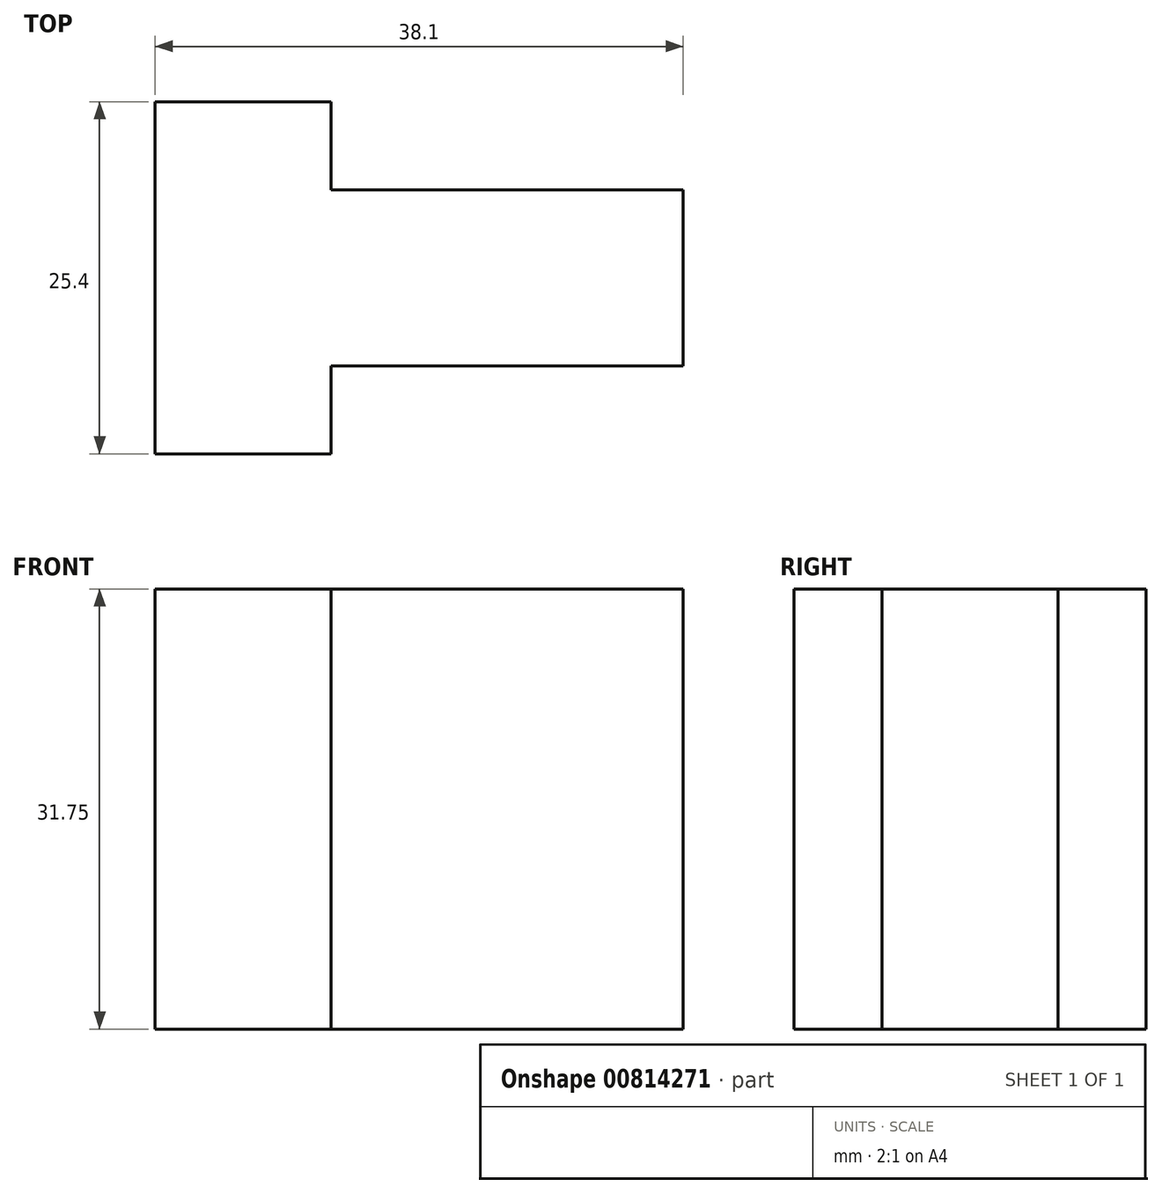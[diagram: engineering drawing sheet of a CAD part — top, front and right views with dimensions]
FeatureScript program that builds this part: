
annotation { "Feature Type Name" : "Feature", "Feature Type Description" : "" }
export const myFeature = defineFeature(function(context is Context, id is Id, definition is map)
    precondition{}
    {
        {
            var Q0;
            Q0=qCreatedBy(makeId("Top.planeOp"),FACE);
            var sketch = newSketch(context, id + "F0", { "sketchPlane" : qUnion([Q0])});
            skLineSegment(sketch, "E0", {"start": v(0, 0) * mm, "end": v(38.1, 0) * mm});
            skLineSegment(sketch, "E1", {"start": v(38.1, 0) * mm, "end": v(38.1, 25.4) * mm});
            skLineSegment(sketch, "E2", {"start": v(0, 0) * mm, "end": v(0, 25.4) * mm});
            skLineSegment(sketch, "E3", {"start": v(38.1, 25.4) * mm, "end": v(0, 25.4) * mm});
            skSolve(sketch);
        }
        {
            var Q0;
            Q0=makeQuery(id+"F0.imprint","IMPRINT",FACE,{"disambiguationData":[TD([[makeQuery(id+"F0.imprint","IMPRINT",EDGE,{"derivedFrom":sQuery(id+"F0.wireOp",EDGE,"E0")}),1.0]])]});
            extrude(context, id + "F1", {"entities" : qUnion([Q0]), "depth" : 31.75 * mm, "offsetDistance" : 25.4 * mm});
        }
        {
            var Q0;
            Q0=makeQuery(id+"F1.opExtrude","SWEPT_FACE",FACE,{"disambiguationData":[OSD([sQuery(id+"F0.wireOp",EDGE,"E1")])]});
            var sketch = newSketch(context, id + "F2", { "sketchPlane" : qUnion([Q0])});
            skLineSegment(sketch, "E4", {"start": v(0, 0) * mm, "end": v(6.35, 0) * mm});
            skLineSegment(sketch, "E5", {"start": v(6.35, 0) * mm, "end": v(6.35, 31.75) * mm});
            skLineSegment(sketch, "E6", {"start": v(6.35, 31.75) * mm, "end": v(0, 31.75) * mm});
            skSolve(sketch);
        }
        {
            var Q0;
            Q0=makeQuery(id+"F2.imprint","IMPRINT",FACE,{"disambiguationData":[TD([[makeQuery(id+"F2.imprint","IMPRINT",EDGE,{"derivedFrom":sQuery(id+"F2.wireOp",EDGE,"E4")}),1.0]])]});
            extrude(context, id + "F3", {"entities" : qUnion([Q0]), "operationType" : NewBodyOperationType.REMOVE, "oppositeDirection" : true, "depth" : 25.4 * mm, "offsetDistance" : 25.4 * mm});
        }
        {
            var Q0;
            Q0=makeQuery(id+"F1.opExtrude","SWEPT_FACE",FACE,{"disambiguationData":[OSD([sQuery(id+"F0.wireOp",EDGE,"E1")])]});
            var sketch = newSketch(context, id + "F4", { "sketchPlane" : qUnion([Q0])});
            skLineSegment(sketch, "E7", {"start": v(25.4, 31.75) * mm, "end": v(19.05, 31.75) * mm});
            skLineSegment(sketch, "E8", {"start": v(25.4, 0) * mm, "end": v(19.05, 0) * mm});
            skLineSegment(sketch, "E9", {"start": v(19.05, 0) * mm, "end": v(19.05, 31.75) * mm});
            skSolve(sketch);
        }
        {
            var Q0;
            Q0=makeQuery(id+"F4.imprint","IMPRINT",FACE,{"disambiguationData":[TD([[makeQuery(id+"F4.imprint","IMPRINT",EDGE,{"derivedFrom":sQuery(id+"F4.wireOp",EDGE,"E7")}),-1.0]])]});
            extrude(context, id + "F5", {"entities" : qUnion([Q0]), "operationType" : NewBodyOperationType.REMOVE, "oppositeDirection" : true, "depth" : 25.4 * mm, "offsetDistance" : 25.4 * mm});
        }
    });
